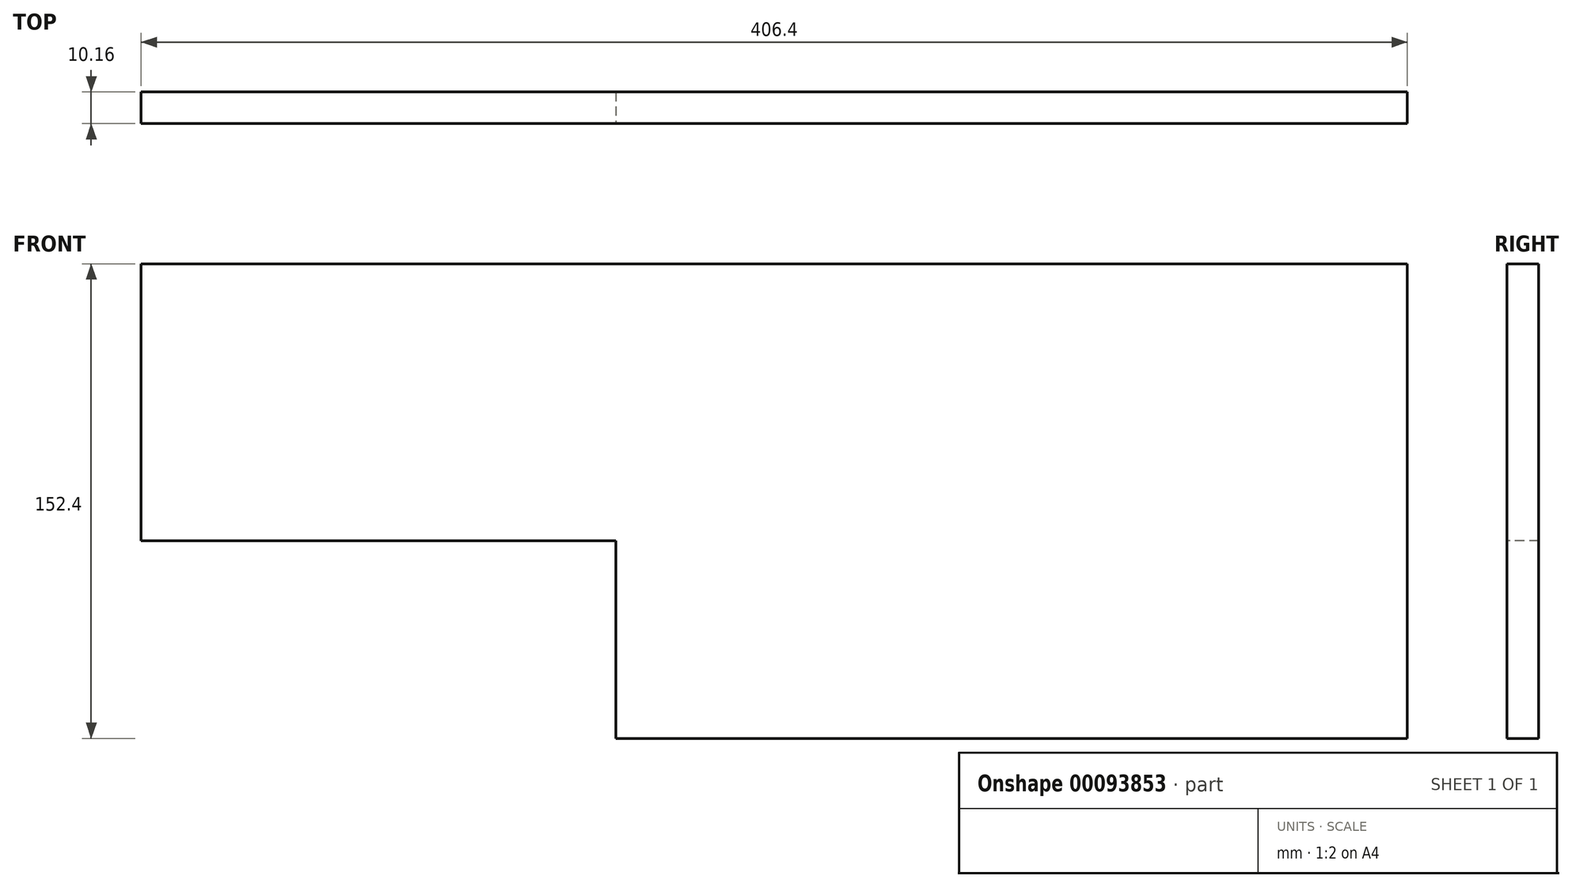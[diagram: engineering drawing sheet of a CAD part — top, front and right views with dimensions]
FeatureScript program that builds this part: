
annotation { "Feature Type Name" : "Feature", "Feature Type Description" : "" }
export const myFeature = defineFeature(function(context is Context, id is Id, definition is map)
    precondition{}
    {
        {
            var Q0;
            Q0=qCreatedBy(makeId("Front.planeOp"),FACE);
            var sketch = newSketch(context, id + "F0", { "sketchPlane" : qUnion([Q0])});
            skLineSegment(sketch, "E0", {"start": v(152.4, 0) * mm, "end": v(406.4, 0) * mm});
            skLineSegment(sketch, "E1", {"start": v(406.4, 0) * mm, "end": v(406.4, 152.4) * mm});
            skLineSegment(sketch, "E2", {"start": v(406.4, 152.4) * mm, "end": v(0, 152.4) * mm});
            skLineSegment(sketch, "E3", {"start": v(0, 152.4) * mm, "end": v(0, 63.5) * mm});
            skLineSegment(sketch, "E4", {"start": v(0, 63.5) * mm, "end": v(152.4, 63.5) * mm});
            skLineSegment(sketch, "E5", {"start": v(152.4, 63.5) * mm, "end": v(152.4, 0) * mm});
            skSolve(sketch);
        }
        {
            var Q0;
            Q0=makeQuery(id+"F0.imprint","IMPRINT",FACE,{"disambiguationData":[TD([[makeQuery(id+"F0.imprint","IMPRINT",EDGE,{"derivedFrom":sQuery(id+"F0.wireOp",EDGE,"E0")}),1.0]])]});
            extrude(context, id + "F1", {"entities" : qUnion([Q0]), "oppositeDirection" : true, "depth" : 10.16 * mm});
        }
    });
